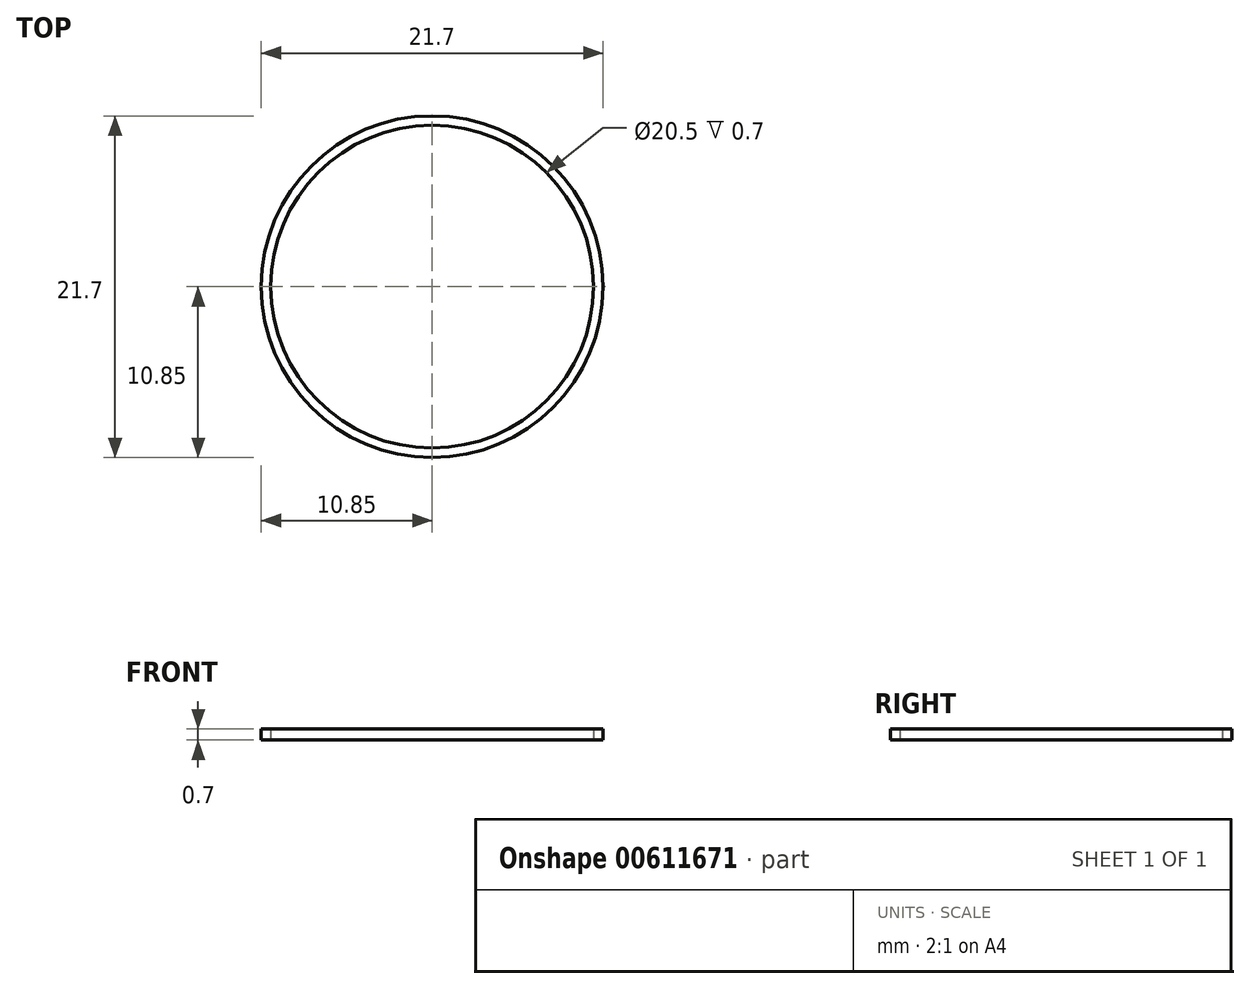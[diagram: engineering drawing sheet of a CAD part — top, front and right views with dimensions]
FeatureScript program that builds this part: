
annotation { "Feature Type Name" : "Feature", "Feature Type Description" : "" }
export const myFeature = defineFeature(function(context is Context, id is Id, definition is map)
    precondition{}
    {
        {
            var Q0;
            Q0=qCreatedBy(makeId("Top.planeOp"),FACE);
            var sketch = newSketch(context, id + "F0", { "sketchPlane" : qUnion([Q0])});
            skCircle(sketch, "E0", {"center": v(0, 0) * mm, "radius": 10.25 * mm});
            skCircle(sketch, "E1", {"center": v(0, 0) * mm, "radius": 10.85 * mm});
            skSolve(sketch);
        }
        {
            var Q0;
            Q0=makeQuery(id+"F0.imprint","IMPRINT",FACE,{"disambiguationData":[TD([[makeQuery(id+"F0.imprint","IMPRINT",EDGE,{"derivedFrom":sQuery(id+"F0.wireOp",EDGE,"E0")}),-1.0]])]});
            extrude(context, id + "F1", {"entities" : qUnion([Q0]), "depth" : 0.7 * mm, "offsetDistance" : 25 * mm});
        }
    });
